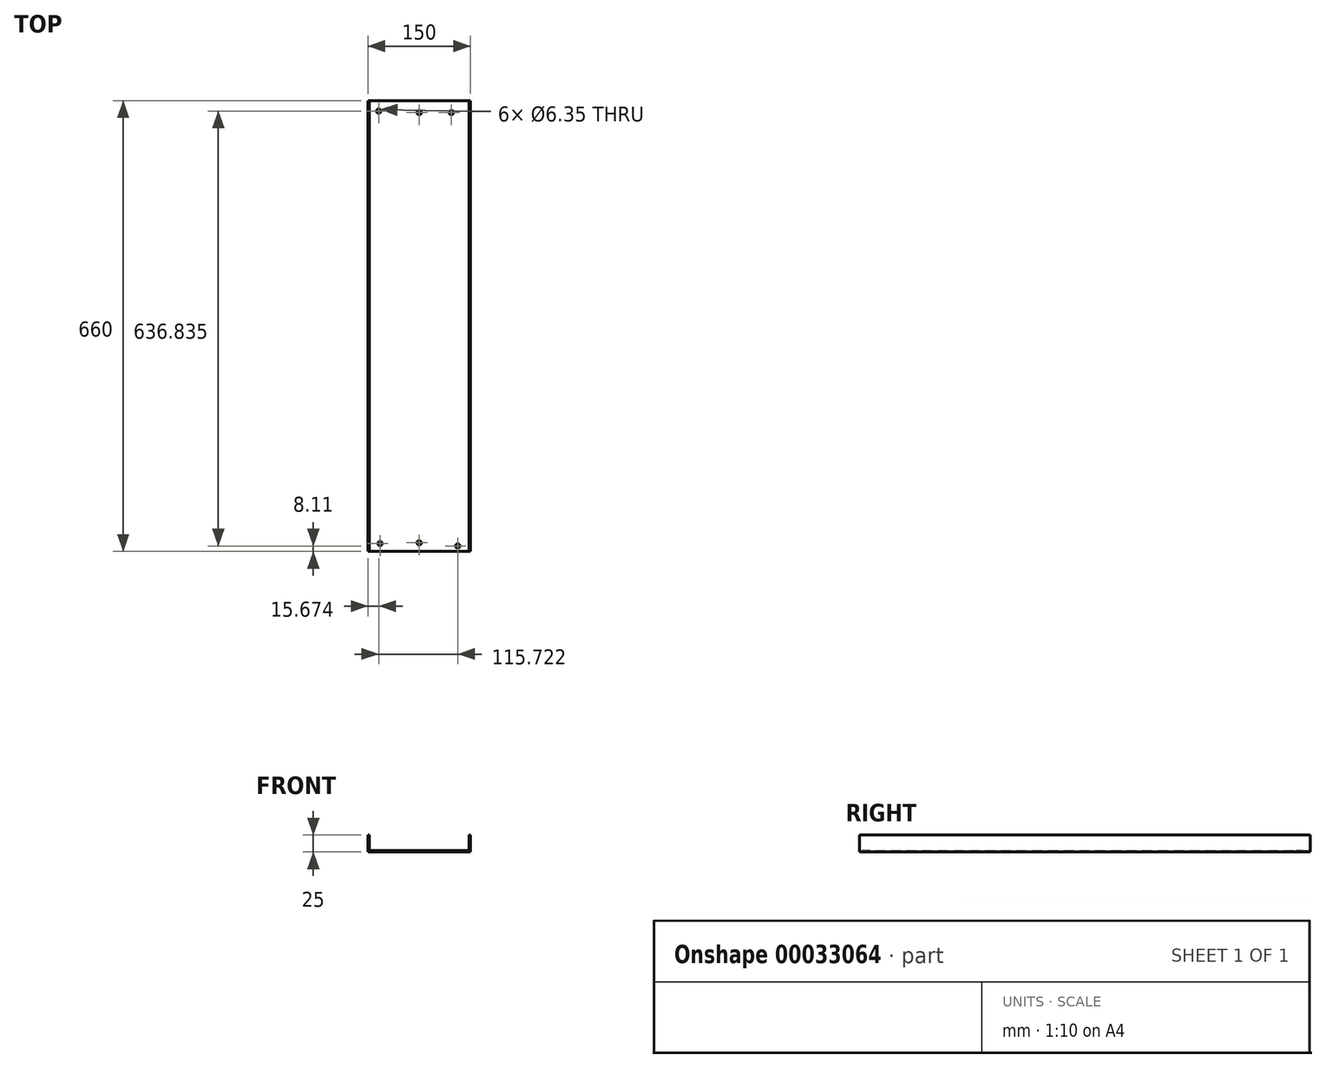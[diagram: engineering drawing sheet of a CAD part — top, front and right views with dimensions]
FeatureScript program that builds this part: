
annotation { "Feature Type Name" : "Feature", "Feature Type Description" : "" }
export const myFeature = defineFeature(function(context is Context, id is Id, definition is map)
    precondition{}
    {
        {
            var Q0;
            Q0=qCreatedBy(makeId("Front.planeOp"),FACE);
            var sketch = newSketch(context, id + "F0", { "sketchPlane" : qUnion([Q0])});
            skLineSegment(sketch, "E0", {"start": v(0, 0) * mm, "end": v(0, -23) * mm});
            skLineSegment(sketch, "E1", {"start": v(0, -23) * mm, "end": v(146, -23) * mm});
            skLineSegment(sketch, "E2", {"start": v(146, -23) * mm, "end": v(146, 0) * mm});
            skLineSegment(sketch, "E3.0", {"start": v(148, -25) * mm, "end": v(148, 0) * mm});
            skLineSegment(sketch, "E3.1", {"start": v(-2, -25) * mm, "end": v(148, -25) * mm});
            skLineSegment(sketch, "E3.2", {"start": v(-2, 0) * mm, "end": v(-2, -25) * mm});
            skLineSegment(sketch, "E4", {"start": v(-2, 0) * mm, "end": v(0, 0) * mm});
            skLineSegment(sketch, "E5", {"start": v(146, 0) * mm, "end": v(148, 0) * mm});
            skSolve(sketch);
        }
        {
            var Q0;
            Q0=makeQuery(id+"F0.imprint","IMPRINT",FACE,{"disambiguationData":[TD([[makeQuery(id+"F0.imprint","IMPRINT",EDGE,{"derivedFrom":sQuery(id+"F0.wireOp",EDGE,"E0")}),-1.0]])]});
            extrude(context, id + "F1", {"entities" : qUnion([Q0]), "depth" : 660 * mm});
        }
        {
            var Q0;
            Q0=makeQuery(id+"F1.opExtrude","SWEPT_FACE",FACE,{"disambiguationData":[OSD([sQuery(id+"F0.wireOp",EDGE,"E1")])]});
            var sketch = newSketch(context, id + "F2", { "sketchPlane" : qUnion([Q0])});
            skPoint(sketch, "E6", {"position": v(15.72, -648.33) * mm});
            skPoint(sketch, "E7", {"position": v(73, -647.24) * mm});
            skPoint(sketch, "E7.positionSnap0", {"position": v(73, -660) * mm});
            skPoint(sketch, "E8", {"position": v(129.4, -651.89) * mm});
            skPoint(sketch, "E9", {"position": v(13.67, -15.05) * mm});
            skPoint(sketch, "E10", {"position": v(73, -17.31) * mm});
            skPoint(sketch, "E10.positionSnap0", {"position": v(73, 0) * mm});
            skPoint(sketch, "E11", {"position": v(120, -17.31) * mm});
            skSolve(sketch);
        }
        {
            var Q0;
            Q0=sQuery(id+"F2.wireOp",VERTEX,"E6");
            var Q1;
            Q1=sQuery(id+"F2.wireOp",VERTEX,"E7");
            var Q2;
            Q2=sQuery(id+"F2.wireOp",VERTEX,"E8");
            var Q3;
            Q3=sQuery(id+"F2.wireOp",VERTEX,"E11");
            var Q4;
            Q4=sQuery(id+"F2.wireOp",VERTEX,"E10");
            var Q5;
            Q5=sQuery(id+"F2.wireOp",VERTEX,"E9");
            var Q6;
            Q6=makeQuery(id+"F1.opExtrude","SWEPT_BODY",BODY,{"disambiguationData":[OSD([sQuery(id+"F0.wireOp",EDGE,"E0"),sQuery(id+"F0.wireOp",EDGE,"E1"),sQuery(id+"F0.wireOp",EDGE,"E2"),sQuery(id+"F0.wireOp",EDGE,"E3.0"),sQuery(id+"F0.wireOp",EDGE,"E3.1"),sQuery(id+"F0.wireOp",EDGE,"E3.2"),sQuery(id+"F0.wireOp",EDGE,"E4"),sQuery(id+"F0.wireOp",EDGE,"E5")])]});
            hole(context, id + "F3", {"style" : HoleStyle.SIMPLE, "holeDiameter" : 6.35 * mm, "endStyle" : HoleEndStyle.THROUGH, "locations" : qUnion([Q0, Q1, Q2, Q3, Q4, Q5]), "scope" : qUnion([Q6])});
        }
    });
